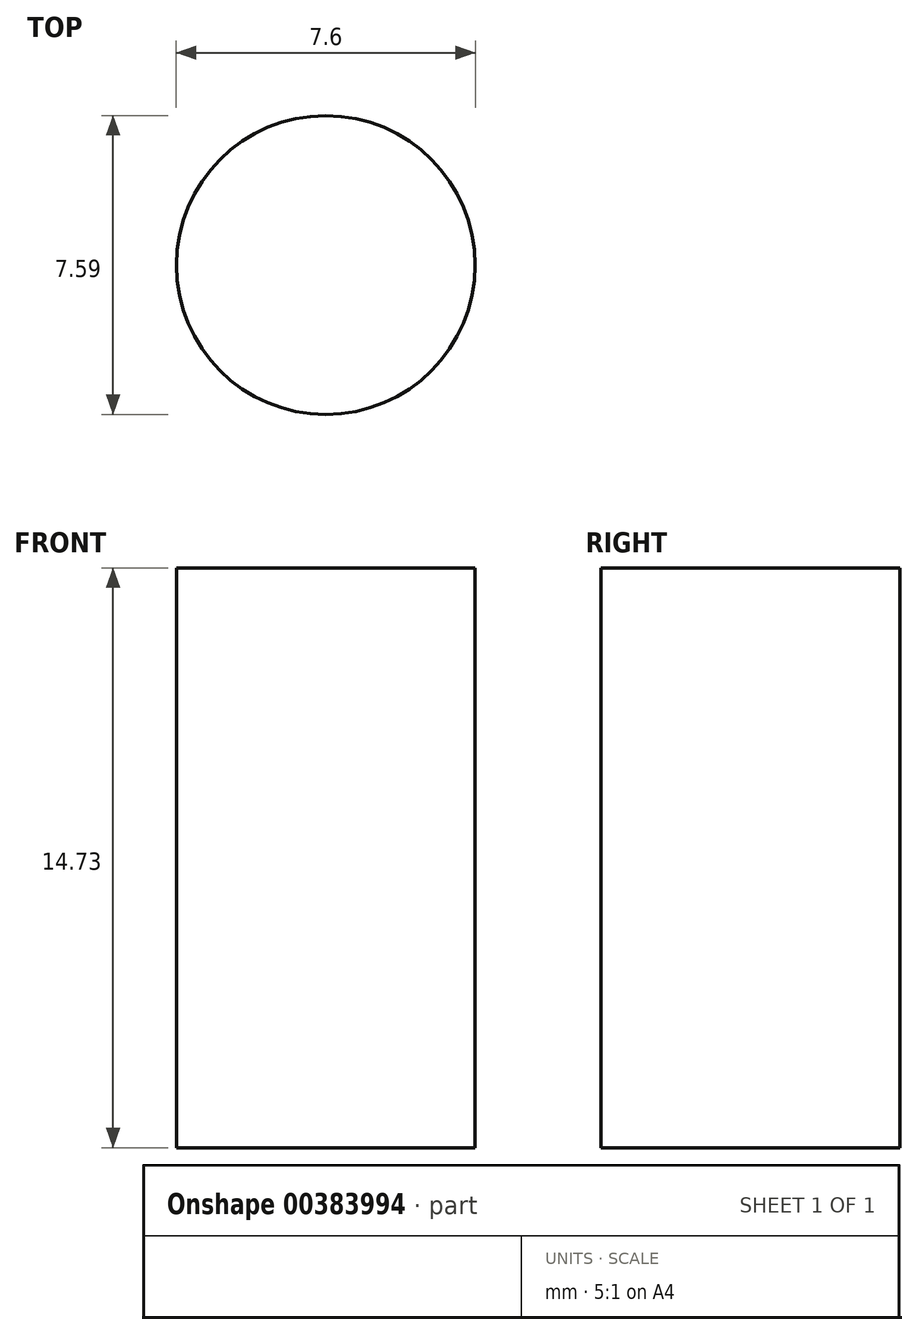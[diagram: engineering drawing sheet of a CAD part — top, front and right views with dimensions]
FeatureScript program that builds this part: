
annotation { "Feature Type Name" : "Feature", "Feature Type Description" : "" }
export const myFeature = defineFeature(function(context is Context, id is Id, definition is map)
    precondition{}
    {
        {
            var Q0;
            Q0=qCreatedBy(makeId("Top.planeOp"),FACE);
            var sketch = newSketch(context, id + "F0", { "sketchPlane" : qUnion([Q0])});
            skCircle(sketch, "E0", {"center": v(0, -2.45) * mm, "radius": 3.8 * mm});
            skSolve(sketch);
        }
        {
            var Q0;
            Q0=makeQuery(id+"F0.imprint","IMPRINT",FACE,{"disambiguationData":[TD([[makeQuery(id+"F0.imprint","IMPRINT",EDGE,{"derivedFrom":sQuery(id+"F0.wireOp",EDGE,"E0")}),1.0]])]});
            extrude(context, id + "F1", {"entities" : qUnion([Q0]), "depth" : 14.73 * mm, "offsetDistance" : 25.4 * mm});
        }
    });
